# Revit family: 57302421
name_source: partatom
category: Plumbing Fixtures
revit_build: Autodesk Revit 2017 (Build: 20190508_0315(x64)
units: mm (PartAtom-declared; Revit-internal decimal feet)

## family parameters
Always vertical = Yes
Cut with Voids When Loaded = No
OmniClass Number = 23.45.55.00
OmniClass Title = Sanitary Faucets, Wastes
Part Type = Normal
Room Calculation Point = No
Round Connector Dimension = Use Diameter
Shared = No
Work Plane-Based = No

## types (1)
- 57302421 Cover part for bath and shower faucet, 75x75 mm
    2D/3D/BIM Files URL = http://static.hansa.com
    Advanced Features = DZR brass;Hose guide, revolving
    Aerator = CACHÉ® integrated aerator;CASCADE®
    AssetType = Fixed
    BIMObjectName = 57302421
    Backflow Prevention EN1717 = AA / EB
    BodyMaterial = Brass
    Brand = Hansa
    Catalog Drawing URL = http://static.hansa.com
    Category = Bathroom
    Class = Trim Kit;Single lever
    CloseOffRating = 0
    Color = Chrome
    ConvergoRefNr = 0087-2006-0021-FI
    Customs Code = 84818011
    Dimension Drawing URL = http://static.hansa.com
    DurationUnit = Year
    EAN Number = 4057304014536
    EN Standard = EN 817
    FDV Document URL = http://www.hansa.com
    FaucetMainMaterial = Brass
    Features = Trim Kit;Single lever
    Finish = Polished
    Flow Drawing URL = http://static.hansa.com
    Flow Rate At 300kPa = 0.3 L/s
    FlowCoefficient = 0
    Group = Bath faucets
    IfcExportAs = IfcValveType
    IfcExportType = FAUCET
    Included = Square rosette
    Installation Type = Rim mounted;Tiled rim assembly
    Installation and Maintenance = http://static.hansa.com
    Lever Handle = ;Lever with H+C symbol;Pin lever
    Manufacturer = Hansa
    ManufacturerName = Hansa
    ManufacturerURL = http://www.hansa.com
    Market = INT;DEU;AUT;BEL;NLD;FRA;CZE;SVK;ITA;ESP
    Material = Brass
    Max. Hot Water Supply = 90 °C
    Mechanical Parts = ;Non-return valve(s);Litter filter(s)
    Model = 57302421 Cover part for bath and shower faucet, 75x75 mm
    ModelReference = 57302421
    Mounting Holes = 4MountingHoles
    NBSDescription = Water supply fittings for baths
    NBSReference = 45-35-70/315
    Name = 57302421 Cover part for bath and shower faucet, 75x75 mm
    Name_en = 57302421 Cover part for bath and shower faucet, 75x75 mm
    NominalDepth = 233 mm
    NominalHeight = 214 mm
    NominalWidth = 435 mm
    Package Weight = 5.08 kg
    Package external Dimensions = 570.0 x 505.0 x 135.0
    Product Code = 57302421
    Product Datasheet = http://www.hansa.com
    Product Family = HANSASTELA
    Product Image URL = http://static.hansa.com
    Product URL = http://static.hansa.com
    Projection = 177 mm
    Shape = Sculptured
    Shower Parts = Hand shower;Shower Hose (1750 mm)
    Shower Spray = Intense
    Shower Spray Number = 1Spray
    Size = 435x235x215 mm
    Spare Parts = http://static.hansa.com
    Technical DataSheet URL = http://www.hansa.com
    Uniclass2 = Pr_40_30_96_07
    Uniclass2015Description = Bath manual water supply sets
    Uniclass2015Reference = Pr_40_20_87_07
    Version = 1
    VersionDate = 06/07/2020
    WarrantyDescription = http://warranty.hansa.com
    WarrantyDurationUnit = Year
    WorkingPressure = 50 - 1000 kPa

## geometry (parser evidence)
native form markers: Sweep x6
no freeform markers — native parametric forms only
